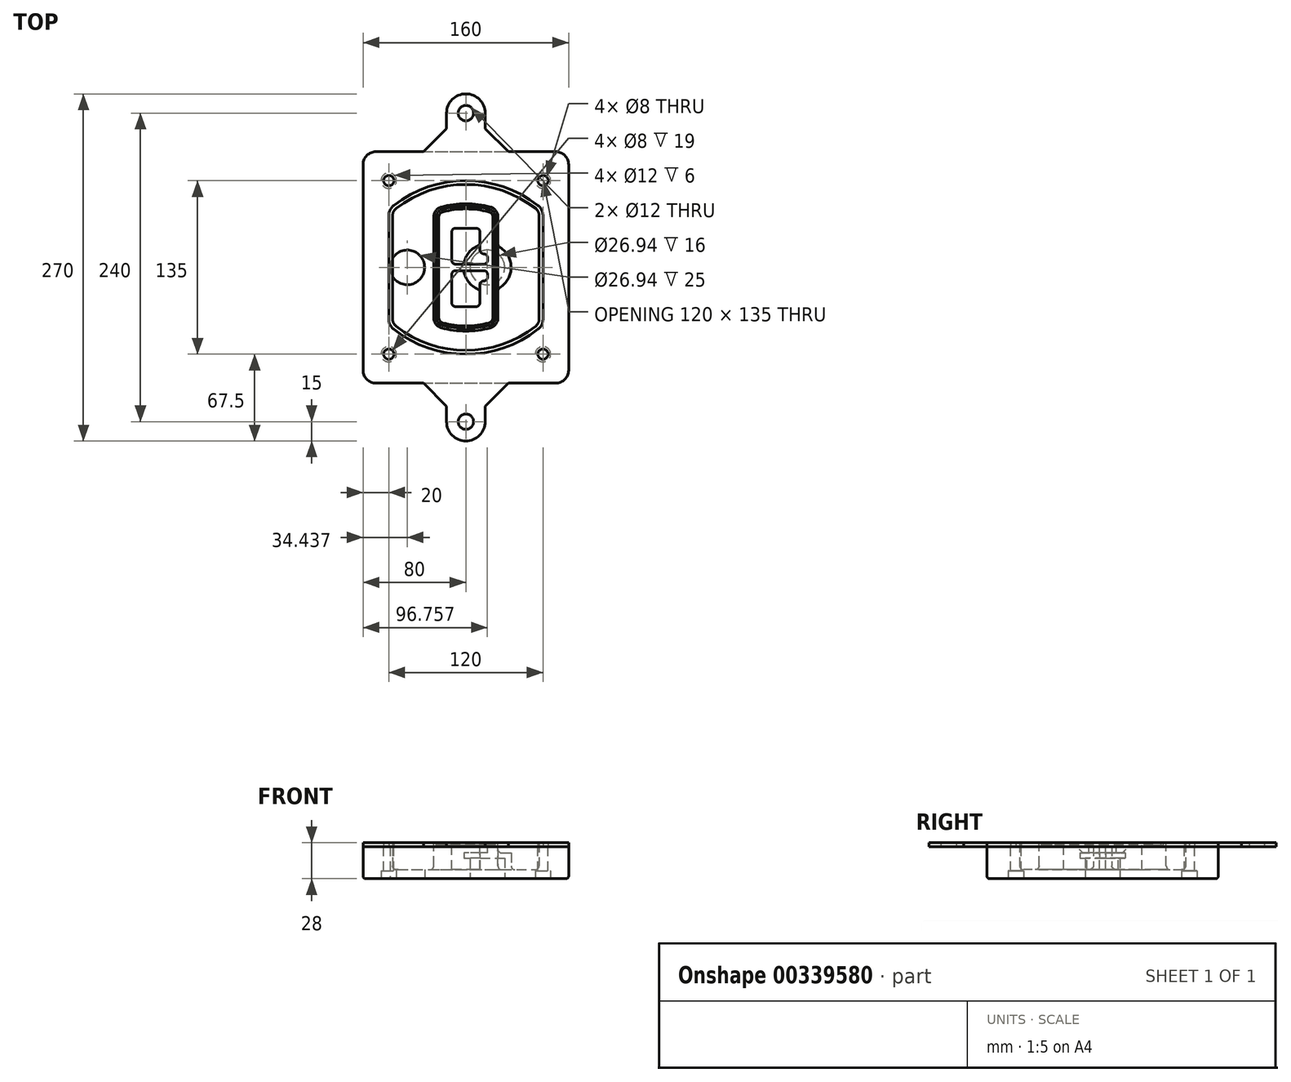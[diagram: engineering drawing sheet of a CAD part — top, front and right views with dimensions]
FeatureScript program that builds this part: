
annotation { "Feature Type Name" : "Feature", "Feature Type Description" : "" }
export const myFeature = defineFeature(function(context is Context, id is Id, definition is map)
    precondition{}
    {
        {
            var Q0;
            Q0=qCreatedBy(makeId("Top.planeOp"),FACE);
            var sketch = newSketch(context, id + "F0", { "sketchPlane" : qUnion([Q0])});
            skPoint(sketch, "E0.rect.middle", {"position": v(0, 0) * mm});
            skLineSegment(sketch, "E1.bottom", {"start": v(-70, -90) * mm, "end": v(70, -90) * mm});
            skLineSegment(sketch, "E1.top", {"start": v(-70, 90) * mm, "end": v(70, 90) * mm});
            skLineSegment(sketch, "E1.left", {"start": v(-80, -80) * mm, "end": v(-80, 80) * mm});
            skLineSegment(sketch, "E1.right", {"start": v(80, -80) * mm, "end": v(80, 80) * mm});
            skLineSegment(sketch, "E2", {"start": v(-80, 90) * mm, "end": v(80, -90) * mm, "construction": true});
            skLineSegment(sketch, "E3", {"start": v(80, 90) * mm, "end": v(-80, -90) * mm, "construction": true});
            skCircle(sketch, "E4", {"center": v(-60, 67.5) * mm, "radius": 4 * mm});
            skCircle(sketch, "E5", {"center": v(60, 67.5) * mm, "radius": 4 * mm});
            skCircle(sketch, "E6", {"center": v(60, -67.5) * mm, "radius": 4 * mm});
            skCircle(sketch, "E7", {"center": v(-60, -67.5) * mm, "radius": 4 * mm});
            skLineSegment(sketch, "E8", {"start": v(-60, 67.5) * mm, "end": v(60, 67.5) * mm, "construction": true});
            skLineSegment(sketch, "E9", {"start": v(60, 67.5) * mm, "end": v(60, -67.5) * mm, "construction": true});
            skLineSegment(sketch, "E10", {"start": v(60, -67.5) * mm, "end": v(-60, -67.5) * mm, "construction": true});
            skLineSegment(sketch, "E11", {"start": v(-60, -67.5) * mm, "end": v(-60, 67.5) * mm, "construction": true});
            skLineSegment(sketch, "E12", {"start": v(-60, 40.3) * mm, "end": v(-60, -40.3) * mm});
            skLineSegment(sketch, "E13", {"start": v(60, 40.3) * mm, "end": v(60, -40.3) * mm});
            skArc(sketch, "E14", {"start": v(56.15, 48.18) * mm, "mid": v(0, 67.5) * mm, "end": v(-56.15, 48.18) * mm});
            skArc(sketch, "E15", {"start": v(-56.15, -48.18) * mm, "mid": v(0, -67.5) * mm, "end": v(56.15, -48.18) * mm});
            skLineSegment(sketch, "E16", {"start": v(-60, 0) * mm, "end": v(60, 0) * mm, "construction": true});
            skPoint(sketch, "E17.visualSharp", {"position": v(-60, -45) * mm});
            skArc(sketch, "E17.filletArc", {"start": v(-60, -40.3) * mm, "mid": v(-58.99, -44.68) * mm, "end": v(-56.15, -48.18) * mm});
            skPoint(sketch, "E18.visualSharp", {"position": v(-60, 45) * mm});
            skArc(sketch, "E18.filletArc", {"start": v(-56.15, 48.18) * mm, "mid": v(-58.99, 44.68) * mm, "end": v(-60, 40.3) * mm});
            skPoint(sketch, "E19.visualSharp", {"position": v(60, 45) * mm});
            skArc(sketch, "E19.filletArc", {"start": v(60, 40.3) * mm, "mid": v(58.99, 44.68) * mm, "end": v(56.15, 48.18) * mm});
            skPoint(sketch, "E20.visualSharp", {"position": v(60, -45) * mm});
            skArc(sketch, "E20.filletArc", {"start": v(56.15, -48.18) * mm, "mid": v(58.99, -44.68) * mm, "end": v(60, -40.3) * mm});
            skPoint(sketch, "E21.visualSharp", {"position": v(-80, 90) * mm});
            skArc(sketch, "E21.filletArc", {"start": v(-70, 90) * mm, "mid": v(-77.07, 87.07) * mm, "end": v(-80, 80) * mm});
            skPoint(sketch, "E22.visualSharp", {"position": v(80, 90) * mm});
            skArc(sketch, "E22.filletArc", {"start": v(80, 80) * mm, "mid": v(77.07, 87.07) * mm, "end": v(70, 90) * mm});
            skPoint(sketch, "E23.visualSharp", {"position": v(80, -90) * mm});
            skArc(sketch, "E23.filletArc", {"start": v(70, -90) * mm, "mid": v(77.07, -87.07) * mm, "end": v(80, -80) * mm});
            skPoint(sketch, "E24.visualSharp", {"position": v(-80, -90) * mm});
            skArc(sketch, "E24.filletArc", {"start": v(-80, -80) * mm, "mid": v(-77.07, -87.07) * mm, "end": v(-70, -90) * mm});
            skArc(sketch, "E25.0", {"start": v(57, 40.3) * mm, "mid": v(56.3, 43.36) * mm, "end": v(54.3, 45.81) * mm});
            skLineSegment(sketch, "E25.1", {"start": v(57, 40.3) * mm, "end": v(57, -40.3) * mm});
            skArc(sketch, "E25.2", {"start": v(54.3, -45.81) * mm, "mid": v(56.3, -43.36) * mm, "end": v(57, -40.3) * mm});
            skArc(sketch, "E25.3", {"start": v(-54.3, -45.81) * mm, "mid": v(0, -64.5) * mm, "end": v(54.3, -45.81) * mm});
            skArc(sketch, "E25.4", {"start": v(-57, -40.3) * mm, "mid": v(-56.3, -43.36) * mm, "end": v(-54.3, -45.81) * mm});
            skArc(sketch, "E25.5", {"start": v(54.3, 45.81) * mm, "mid": v(0, 64.5) * mm, "end": v(-54.3, 45.81) * mm});
            skLineSegment(sketch, "E25.6", {"start": v(-57, 40.3) * mm, "end": v(-57, -40.3) * mm});
            skArc(sketch, "E25.7", {"start": v(-54.3, 45.81) * mm, "mid": v(-56.3, 43.36) * mm, "end": v(-57, 40.3) * mm});
            skArc(sketch, "E26.0", {"start": v(-58.62, 51.33) * mm, "mid": v(-62.58, 46.43) * mm, "end": v(-64, 40.3) * mm});
            skArc(sketch, "E26.1", {"start": v(58.62, 51.33) * mm, "mid": v(0, 71.5) * mm, "end": v(-58.62, 51.33) * mm});
            skArc(sketch, "E26.2", {"start": v(64, 40.3) * mm, "mid": v(62.58, 46.43) * mm, "end": v(58.62, 51.33) * mm});
            skLineSegment(sketch, "E26.3", {"start": v(64, 40.3) * mm, "end": v(64, -40.3) * mm});
            skArc(sketch, "E26.4", {"start": v(58.62, -51.33) * mm, "mid": v(62.58, -46.43) * mm, "end": v(64, -40.3) * mm});
            skLineSegment(sketch, "E26.5", {"start": v(-64, 40.3) * mm, "end": v(-64, -40.3) * mm});
            skArc(sketch, "E26.6", {"start": v(-58.62, -51.33) * mm, "mid": v(0, -71.5) * mm, "end": v(58.62, -51.33) * mm});
            skArc(sketch, "E26.7", {"start": v(-64, -40.3) * mm, "mid": v(-62.58, -46.43) * mm, "end": v(-58.62, -51.33) * mm});
            skSolve(sketch);
        }
        {
            var Q0;
            Q0=makeQuery(id+"F0.imprint","IMPRINT",FACE,{"disambiguationData":[TD([[makeQuery(id+"F0.imprint","IMPRINT",EDGE,{"derivedFrom":sQuery(id+"F0.wireOp",EDGE,"E1.bottom")}),1.0]])]});
            var Q1;
            Q1=makeQuery(id+"F0.imprint","IMPRINT",FACE,{"disambiguationData":[TD([[makeQuery(id+"F0.imprint","IMPRINT",EDGE,{"derivedFrom":sQuery(id+"F0.wireOp",EDGE,"E12")}),1.0]])]});
            var Q2;
            Q2=makeQuery(id+"F0.imprint","IMPRINT",FACE,{"disambiguationData":[TD([[makeQuery(id+"F0.imprint","IMPRINT",EDGE,{"derivedFrom":sQuery(id+"F0.wireOp",EDGE,"E25.0")}),1.0]])]});
            var Q3;
            Q3=makeQuery(id+"F0.imprint","IMPRINT",FACE,{"disambiguationData":[TD([[makeQuery(id+"F0.imprint","IMPRINT",EDGE,{"derivedFrom":sQuery(id+"F0.wireOp",EDGE,"E12")}),-1.0]])]});
            extrude(context, id + "F1", {"entities" : qUnion([Q0, Q1, Q2, Q3]), "oppositeDirection" : true, "depth" : 25 * mm});
        }
        {
            var Q0;
            Q0=makeQuery(id+"F0.imprint","IMPRINT",FACE,{"disambiguationData":[TD([[makeQuery(id+"F0.imprint","IMPRINT",EDGE,{"derivedFrom":sQuery(id+"F0.wireOp",EDGE,"E12")}),1.0]])]});
            extrude(context, id + "F2", {"entities" : qUnion([Q0]), "operationType" : NewBodyOperationType.ADD, "depth" : 3 * mm});
        }
        {
            var Q0;
            Q0=makeQuery(id+"F0.imprint","IMPRINT",FACE,{"disambiguationData":[TD([[makeQuery(id+"F0.imprint","IMPRINT",EDGE,{"derivedFrom":sQuery(id+"F0.wireOp",EDGE,"E25.0")}),1.0]])]});
            extrude(context, id + "F3", {"entities" : qUnion([Q0]), "operationType" : NewBodyOperationType.REMOVE, "oppositeDirection" : true, "depth" : 18 * mm});
        }
        {
            var Q0;
            Q0=makeQuery(id+"F2.opExtrude","CAP_FACE",FACE,{"disambiguationData":[OSD([sQuery(id+"F0.wireOp",EDGE,"E12"),sQuery(id+"F0.wireOp",EDGE,"E13"),sQuery(id+"F0.wireOp",EDGE,"E14"),sQuery(id+"F0.wireOp",EDGE,"E15"),sQuery(id+"F0.wireOp",EDGE,"E17.filletArc"),sQuery(id+"F0.wireOp",EDGE,"E18.filletArc"),sQuery(id+"F0.wireOp",EDGE,"E19.filletArc"),sQuery(id+"F0.wireOp",EDGE,"E20.filletArc"),sQuery(id+"F0.wireOp",EDGE,"E25.0"),sQuery(id+"F0.wireOp",EDGE,"E25.1"),sQuery(id+"F0.wireOp",EDGE,"E25.2"),sQuery(id+"F0.wireOp",EDGE,"E25.3"),sQuery(id+"F0.wireOp",EDGE,"E25.4"),sQuery(id+"F0.wireOp",EDGE,"E25.5"),sQuery(id+"F0.wireOp",EDGE,"E25.6"),sQuery(id+"F0.wireOp",EDGE,"E25.7")])],"isStart":false});
            var sketch = newSketch(context, id + "F4", { "sketchPlane" : qUnion([Q0])});
            skArc(sketch, "E27.0", {"start": v(-19.08, -46.97) * mm, "mid": v(0, -49.5) * mm, "end": v(19.08, -46.97) * mm});
            skArc(sketch, "E28.0", {"start": v(19.08, 46.97) * mm, "mid": v(0, 49.5) * mm, "end": v(-19.08, 46.97) * mm});
            skLineSegment(sketch, "E29", {"start": v(-25, 39.25) * mm, "end": v(-25, -39.25) * mm});
            skLineSegment(sketch, "E30", {"start": v(25, 39.25) * mm, "end": v(25, -39.25) * mm});
            skLineSegment(sketch, "E31", {"start": v(-25, 45.1) * mm, "end": v(25, 45.1) * mm, "construction": true});
            skLineSegment(sketch, "E32", {"start": v(-25, -45.1) * mm, "end": v(25, -45.1) * mm, "construction": true});
            skPoint(sketch, "E33.visualSharp", {"position": v(-25, 45.1) * mm});
            skArc(sketch, "E33.filletArc", {"start": v(-19.08, 46.97) * mm, "mid": v(-23.35, 44.11) * mm, "end": v(-25, 39.25) * mm});
            skPoint(sketch, "E34.visualSharp", {"position": v(25, 45.1) * mm});
            skArc(sketch, "E34.filletArc", {"start": v(25, 39.25) * mm, "mid": v(23.35, 44.11) * mm, "end": v(19.08, 46.97) * mm});
            skPoint(sketch, "E35.visualSharp", {"position": v(25, -45.1) * mm});
            skArc(sketch, "E35.filletArc", {"start": v(19.08, -46.97) * mm, "mid": v(23.35, -44.11) * mm, "end": v(25, -39.25) * mm});
            skPoint(sketch, "E36.visualSharp", {"position": v(-25, -45.1) * mm});
            skArc(sketch, "E36.filletArc", {"start": v(-25, -39.25) * mm, "mid": v(-23.35, -44.11) * mm, "end": v(-19.08, -46.97) * mm});
            skArc(sketch, "E37.0", {"start": v(54.3, 45.81) * mm, "mid": v(0, 64.5) * mm, "end": v(-54.3, 45.81) * mm});
            skArc(sketch, "E37.1", {"start": v(-54.3, 45.81) * mm, "mid": v(-56.3, 43.36) * mm, "end": v(-57, 40.3) * mm});
            skLineSegment(sketch, "E37.2", {"start": v(-57, 40.3) * mm, "end": v(-57, -40.3) * mm});
            skArc(sketch, "E37.3", {"start": v(-57, -40.3) * mm, "mid": v(-56.3, -43.36) * mm, "end": v(-54.3, -45.81) * mm});
            skArc(sketch, "E37.4", {"start": v(-54.3, -45.81) * mm, "mid": v(0, -64.5) * mm, "end": v(54.3, -45.81) * mm});
            skArc(sketch, "E37.5", {"start": v(54.3, -45.81) * mm, "mid": v(56.3, -43.36) * mm, "end": v(57, -40.3) * mm});
            skLineSegment(sketch, "E37.6", {"start": v(57, 40.3) * mm, "end": v(57, -40.3) * mm});
            skArc(sketch, "E37.7", {"start": v(57, 40.3) * mm, "mid": v(56.3, 43.36) * mm, "end": v(54.3, 45.81) * mm});
            skLineSegment(sketch, "E38.0", {"start": v(23, 39.25) * mm, "end": v(23, -39.25) * mm});
            skArc(sketch, "E38.1", {"start": v(18.56, -45.04) * mm, "mid": v(21.76, -42.9) * mm, "end": v(23, -39.25) * mm});
            skArc(sketch, "E38.2", {"start": v(-18.56, -45.04) * mm, "mid": v(0, -47.5) * mm, "end": v(18.56, -45.04) * mm});
            skArc(sketch, "E38.3", {"start": v(-23, -39.25) * mm, "mid": v(-21.76, -42.9) * mm, "end": v(-18.56, -45.04) * mm});
            skLineSegment(sketch, "E38.4", {"start": v(-23, 39.25) * mm, "end": v(-23, -39.25) * mm});
            skArc(sketch, "E38.5", {"start": v(23, 39.25) * mm, "mid": v(21.76, 42.9) * mm, "end": v(18.56, 45.04) * mm});
            skArc(sketch, "E38.6", {"start": v(-18.56, 45.04) * mm, "mid": v(-21.76, 42.9) * mm, "end": v(-23, 39.25) * mm});
            skArc(sketch, "E38.7", {"start": v(18.56, 45.04) * mm, "mid": v(0, 47.5) * mm, "end": v(-18.56, 45.04) * mm});
            skArc(sketch, "E39.0", {"start": v(21, 39.25) * mm, "mid": v(20.18, 41.68) * mm, "end": v(18.04, 43.1) * mm});
            skLineSegment(sketch, "E39.1", {"start": v(21, 39.25) * mm, "end": v(21, -39.25) * mm});
            skArc(sketch, "E39.2", {"start": v(18.04, -43.1) * mm, "mid": v(20.18, -41.68) * mm, "end": v(21, -39.25) * mm});
            skArc(sketch, "E39.3", {"start": v(-18.04, -43.1) * mm, "mid": v(0, -45.5) * mm, "end": v(18.04, -43.1) * mm});
            skArc(sketch, "E39.4", {"start": v(-21, -39.25) * mm, "mid": v(-20.18, -41.68) * mm, "end": v(-18.04, -43.1) * mm});
            skArc(sketch, "E39.5", {"start": v(18.04, 43.1) * mm, "mid": v(0, 45.5) * mm, "end": v(-18.04, 43.1) * mm});
            skLineSegment(sketch, "E39.6", {"start": v(-21, 39.25) * mm, "end": v(-21, -39.25) * mm});
            skArc(sketch, "E39.7", {"start": v(-18.04, 43.1) * mm, "mid": v(-20.18, 41.68) * mm, "end": v(-21, 39.25) * mm});
            skLineSegment(sketch, "E40", {"start": v(-25, 0) * mm, "end": v(25, 0) * mm, "construction": true});
            skLineSegment(sketch, "E41", {"start": v(-11, 5.5) * mm, "end": v(-11, 27.5) * mm});
            skLineSegment(sketch, "E42", {"start": v(-8, 30.5) * mm, "end": v(8, 30.5) * mm});
            skLineSegment(sketch, "E43", {"start": v(11, 27.5) * mm, "end": v(11, 13.5) * mm});
            skLineSegment(sketch, "E44", {"start": v(14, 10.5) * mm, "end": v(14, 10.5) * mm});
            skLineSegment(sketch, "E45", {"start": v(17, 7.5) * mm, "end": v(17, 5.5) * mm});
            skLineSegment(sketch, "E46", {"start": v(14, 2.5) * mm, "end": v(-8, 2.5) * mm});
            skPoint(sketch, "E47.visualSharp", {"position": v(-11, 30.5) * mm});
            skArc(sketch, "E47.filletArc", {"start": v(-8, 30.5) * mm, "mid": v(-10.12, 29.62) * mm, "end": v(-11, 27.5) * mm});
            skPoint(sketch, "E48.visualSharp", {"position": v(11, 30.5) * mm});
            skArc(sketch, "E48.filletArc", {"start": v(11, 27.5) * mm, "mid": v(10.12, 29.62) * mm, "end": v(8, 30.5) * mm});
            skPoint(sketch, "E49.visualSharp", {"position": v(11, 10.5) * mm});
            skArc(sketch, "E49.filletArc", {"start": v(11, 13.5) * mm, "mid": v(11.88, 11.38) * mm, "end": v(14, 10.5) * mm});
            skPoint(sketch, "E50.visualSharp", {"position": v(17, 10.5) * mm});
            skArc(sketch, "E50.filletArc", {"start": v(17, 7.5) * mm, "mid": v(16.12, 9.62) * mm, "end": v(14, 10.5) * mm});
            skPoint(sketch, "E51.visualSharp", {"position": v(17, 2.5) * mm});
            skArc(sketch, "E51.filletArc", {"start": v(14, 2.5) * mm, "mid": v(16.12, 3.38) * mm, "end": v(17, 5.5) * mm});
            skPoint(sketch, "E52.visualSharp", {"position": v(-11, 2.5) * mm});
            skArc(sketch, "E52.filletArc", {"start": v(-11, 5.5) * mm, "mid": v(-10.12, 3.38) * mm, "end": v(-8, 2.5) * mm});
            skLineSegment(sketch, "E53.0.MirrorCS", {"start": v(14, -2.5) * mm, "end": v(-8, -2.5) * mm});
            skArc(sketch, "E54.0.MirrorCS", {"start": v(-11, -5.5) * mm, "mid": v(-10.12, -3.38) * mm, "end": v(-8, -2.5) * mm});
            skLineSegment(sketch, "E55.0.MirrorCS", {"start": v(-11, -5.5) * mm, "end": v(-11, -27.5) * mm});
            skArc(sketch, "E56.0.MirrorCS", {"start": v(-8, -30.5) * mm, "mid": v(-10.12, -29.62) * mm, "end": v(-11, -27.5) * mm});
            skLineSegment(sketch, "E57.0.MirrorCS", {"start": v(-8, -30.5) * mm, "end": v(8, -30.5) * mm});
            skArc(sketch, "E58.0.MirrorCS", {"start": v(11, -27.5) * mm, "mid": v(10.12, -29.62) * mm, "end": v(8, -30.5) * mm});
            skLineSegment(sketch, "E59.0.MirrorCS", {"start": v(11, -27.5) * mm, "end": v(11, -13.5) * mm});
            skArc(sketch, "E60.0.MirrorCS", {"start": v(11, -13.5) * mm, "mid": v(11.88, -11.38) * mm, "end": v(14, -10.5) * mm});
            skArc(sketch, "E61.0.MirrorCS", {"start": v(17, -7.5) * mm, "mid": v(16.12, -9.62) * mm, "end": v(14, -10.5) * mm});
            skLineSegment(sketch, "E62.0.MirrorCS", {"start": v(17, -7.5) * mm, "end": v(17, -5.5) * mm});
            skArc(sketch, "E63.0.MirrorCS", {"start": v(14, -2.5) * mm, "mid": v(16.12, -3.38) * mm, "end": v(17, -5.5) * mm});
            skSolve(sketch);
        }
        {
            var Q0;
            Q0=makeQuery(id+"F4.imprint","IMPRINT",FACE,{"disambiguationData":[TD([[makeQuery(id+"F4.imprint","IMPRINT",EDGE,{"derivedFrom":sQuery(id+"F4.wireOp",EDGE,"E27.0")}),1.0]])]});
            var Q1;
            Q1=makeQuery(id+"F4.imprint","IMPRINT",FACE,{"disambiguationData":[TD([[makeQuery(id+"F4.imprint","IMPRINT",EDGE,{"derivedFrom":sQuery(id+"F4.wireOp",EDGE,"E38.0")}),-1.0]])]});
            var Q2;
            Q2=makeQuery(id+"F4.imprint","IMPRINT",FACE,{"disambiguationData":[TD([[makeQuery(id+"F4.imprint","IMPRINT",EDGE,{"derivedFrom":sQuery(id+"F4.wireOp",EDGE,"E39.0")}),1.0]])]});
            extrude(context, id + "F5", {"entities" : qUnion([Q0, Q1, Q2]), "operationType" : NewBodyOperationType.ADD, "endBound" : BoundingType.UP_TO_NEXT, "oppositeDirection" : true, "depth" : 25 * mm});
        }
        {
            var Q0;
            Q0=makeQuery(id+"F4.imprint","IMPRINT",FACE,{"disambiguationData":[TD([[makeQuery(id+"F4.imprint","IMPRINT",EDGE,{"derivedFrom":sQuery(id+"F4.wireOp",EDGE,"E38.0")}),-1.0]])]});
            extrude(context, id + "F6", {"entities" : qUnion([Q0]), "operationType" : NewBodyOperationType.REMOVE, "oppositeDirection" : true, "depth" : 2 * mm});
        }
        {
            var Q0;
            Q0=makeQuery(id+"F1.opExtrude","CAP_FACE",FACE,{"disambiguationData":[OSD([sQuery(id+"F0.wireOp",EDGE,"E1.bottom"),sQuery(id+"F0.wireOp",EDGE,"E1.top"),sQuery(id+"F0.wireOp",EDGE,"E1.left"),sQuery(id+"F0.wireOp",EDGE,"E1.right"),sQuery(id+"F0.wireOp",EDGE,"E4"),sQuery(id+"F0.wireOp",EDGE,"E5"),sQuery(id+"F0.wireOp",EDGE,"E6"),sQuery(id+"F0.wireOp",EDGE,"E7"),sQuery(id+"F0.wireOp",EDGE,"E21.filletArc"),sQuery(id+"F0.wireOp",EDGE,"E22.filletArc"),sQuery(id+"F0.wireOp",EDGE,"E23.filletArc"),sQuery(id+"F0.wireOp",EDGE,"E24.filletArc")])],"isStart":false});
            var sketch = newSketch(context, id + "F7", { "sketchPlane" : qUnion([Q0])});
            skCircle(sketch, "E64", {"center": v(16.76, 0) * mm, "radius": 13.47 * mm});
            skCircle(sketch, "E65", {"center": v(-45.56, 0) * mm, "radius": 13.47 * mm});
            skLineSegment(sketch, "E66", {"start": v(80, 0) * mm, "end": v(-80, 0) * mm});
            skCircle(sketch, "E67", {"center": v(16.76, 0) * mm, "radius": 18.47 * mm});
            skCircle(sketch, "E68", {"center": v(60, -67.5) * mm, "radius": 6 * mm});
            skCircle(sketch, "E69", {"center": v(-60, -67.5) * mm, "radius": 6 * mm});
            skCircle(sketch, "E70", {"center": v(-60, 67.5) * mm, "radius": 6 * mm});
            skCircle(sketch, "E71", {"center": v(60, 67.5) * mm, "radius": 6 * mm});
            skSolve(sketch);
        }
        {
            var Q0;
            {var subQ1=sQuery(id+"F7.wireOp",EDGE,"E66");var subQ4=sQuery(id+"F7.wireOp",EDGE,"E64");var subQ6=makeQuery(id+"F7.imprint","INTERSECT",VERTEX,{"disambiguationData":[OD(0.0)],"derivedFrom":[subQ4,subQ1]});Q0=makeQuery(id+"F7.imprint","IMPRINT",FACE,{"disambiguationData":[TD([[makeQuery(id+"F7.imprint","IMPRINT",EDGE,{"disambiguationData":[TD([[subQ6,-1.0]])],"derivedFrom":subQ4}),-1.0]])]});}
            var Q1;
            {var subQ0=sQuery(id+"F7.wireOp",EDGE,"E66");var subQ1=sQuery(id+"F7.wireOp",EDGE,"E64");var subQ3=makeQuery(id+"F7.imprint","INTERSECT",VERTEX,{"disambiguationData":[OD(0.0)],"derivedFrom":[subQ1,subQ0]});Q1=makeQuery(id+"F7.imprint","IMPRINT",FACE,{"disambiguationData":[TD([[makeQuery(id+"F7.imprint","IMPRINT",EDGE,{"disambiguationData":[TD([[subQ3,-1.0]])],"derivedFrom":subQ1}),1.0]])]});}
            var Q2;
            {var subQ0=sQuery(id+"F7.wireOp",EDGE,"E66");var subQ1=sQuery(id+"F7.wireOp",EDGE,"E64");var subQ3=makeQuery(id+"F7.imprint","INTERSECT",VERTEX,{"disambiguationData":[OD(0.0)],"derivedFrom":[subQ1,subQ0]});Q2=makeQuery(id+"F7.imprint","IMPRINT",FACE,{"disambiguationData":[TD([[makeQuery(id+"F7.imprint","IMPRINT",EDGE,{"disambiguationData":[TD([[subQ3,1.0]])],"derivedFrom":subQ1}),1.0]])]});}
            var Q3;
            {var subQ1=sQuery(id+"F7.wireOp",EDGE,"E66");var subQ4=sQuery(id+"F7.wireOp",EDGE,"E64");var subQ6=makeQuery(id+"F7.imprint","INTERSECT",VERTEX,{"disambiguationData":[OD(0.0)],"derivedFrom":[subQ4,subQ1]});Q3=makeQuery(id+"F7.imprint","IMPRINT",FACE,{"disambiguationData":[TD([[makeQuery(id+"F7.imprint","IMPRINT",EDGE,{"disambiguationData":[TD([[subQ6,1.0]])],"derivedFrom":subQ4}),-1.0]])]});}
            extrude(context, id + "F8", {"entities" : qUnion([Q0, Q1, Q2, Q3]), "operationType" : NewBodyOperationType.ADD, "oppositeDirection" : true, "depth" : 20 * mm});
        }
        {
            var Q0;
            {var subQ0=sQuery(id+"F7.wireOp",EDGE,"E66");var subQ1=sQuery(id+"F7.wireOp",EDGE,"E64");var subQ3=makeQuery(id+"F7.imprint","INTERSECT",VERTEX,{"disambiguationData":[OD(0.0)],"derivedFrom":[subQ1,subQ0]});Q0=makeQuery(id+"F7.imprint","IMPRINT",FACE,{"disambiguationData":[TD([[makeQuery(id+"F7.imprint","IMPRINT",EDGE,{"disambiguationData":[TD([[subQ3,-1.0]])],"derivedFrom":subQ1}),1.0]])]});}
            var Q1;
            {var subQ0=sQuery(id+"F7.wireOp",EDGE,"E66");var subQ1=sQuery(id+"F7.wireOp",EDGE,"E64");var subQ3=makeQuery(id+"F7.imprint","INTERSECT",VERTEX,{"disambiguationData":[OD(0.0)],"derivedFrom":[subQ1,subQ0]});Q1=makeQuery(id+"F7.imprint","IMPRINT",FACE,{"disambiguationData":[TD([[makeQuery(id+"F7.imprint","IMPRINT",EDGE,{"disambiguationData":[TD([[subQ3,1.0]])],"derivedFrom":subQ1}),1.0]])]});}
            extrude(context, id + "F9", {"entities" : qUnion([Q0, Q1]), "operationType" : NewBodyOperationType.REMOVE, "oppositeDirection" : true, "depth" : 16 * mm});
        }
        {
            var Q0;
            {var subQ0=sQuery(id+"F7.wireOp",EDGE,"E66");var subQ1=sQuery(id+"F7.wireOp",EDGE,"E65");var subQ3=makeQuery(id+"F7.imprint","INTERSECT",VERTEX,{"disambiguationData":[OD(0.0)],"derivedFrom":[subQ1,subQ0]});Q0=makeQuery(id+"F7.imprint","IMPRINT",FACE,{"disambiguationData":[TD([[makeQuery(id+"F7.imprint","IMPRINT",EDGE,{"disambiguationData":[TD([[subQ3,-1.0]])],"derivedFrom":subQ1}),1.0]])]});}
            var Q1;
            {var subQ0=sQuery(id+"F7.wireOp",EDGE,"E66");var subQ1=sQuery(id+"F7.wireOp",EDGE,"E65");var subQ3=makeQuery(id+"F7.imprint","INTERSECT",VERTEX,{"disambiguationData":[OD(0.0)],"derivedFrom":[subQ1,subQ0]});Q1=makeQuery(id+"F7.imprint","IMPRINT",FACE,{"disambiguationData":[TD([[makeQuery(id+"F7.imprint","IMPRINT",EDGE,{"disambiguationData":[TD([[subQ3,1.0]])],"derivedFrom":subQ1}),1.0]])]});}
            extrude(context, id + "F10", {"entities" : qUnion([Q0, Q1]), "operationType" : NewBodyOperationType.REMOVE, "oppositeDirection" : true, "depth" : 25 * mm});
        }
        {
            var Q0;
            Q0=makeQuery(id+"F7.imprint","IMPRINT",FACE,{"disambiguationData":[TD([[makeQuery(id+"F7.imprint","IMPRINT",EDGE,{"derivedFrom":sQuery(id+"F7.wireOp",EDGE,"E68")}),1.0]])]});
            var Q1;
            Q1=makeQuery(id+"F7.imprint","IMPRINT",FACE,{"disambiguationData":[TD([[makeQuery(id+"F7.imprint","IMPRINT",EDGE,{"derivedFrom":makeQuery(id+"F1.opExtrude","CAP_EDGE",EDGE,{"disambiguationData":[OSD([sQuery(id+"F0.wireOp",EDGE,"E5")])],"isStart":false})}),-1.0]])]});
            var Q2;
            Q2=makeQuery(id+"F7.imprint","IMPRINT",FACE,{"disambiguationData":[TD([[makeQuery(id+"F7.imprint","IMPRINT",EDGE,{"derivedFrom":sQuery(id+"F7.wireOp",EDGE,"E69")}),1.0]])]});
            var Q3;
            Q3=makeQuery(id+"F7.imprint","IMPRINT",FACE,{"disambiguationData":[TD([[makeQuery(id+"F7.imprint","IMPRINT",EDGE,{"derivedFrom":makeQuery(id+"F1.opExtrude","CAP_EDGE",EDGE,{"disambiguationData":[OSD([sQuery(id+"F0.wireOp",EDGE,"E4")])],"isStart":false})}),-1.0]])]});
            var Q4;
            Q4=makeQuery(id+"F7.imprint","IMPRINT",FACE,{"disambiguationData":[TD([[makeQuery(id+"F7.imprint","IMPRINT",EDGE,{"derivedFrom":sQuery(id+"F7.wireOp",EDGE,"E70")}),1.0]])]});
            var Q5;
            Q5=makeQuery(id+"F7.imprint","IMPRINT",FACE,{"disambiguationData":[TD([[makeQuery(id+"F7.imprint","IMPRINT",EDGE,{"derivedFrom":makeQuery(id+"F1.opExtrude","CAP_EDGE",EDGE,{"disambiguationData":[OSD([sQuery(id+"F0.wireOp",EDGE,"E7")])],"isStart":false})}),-1.0]])]});
            var Q6;
            Q6=makeQuery(id+"F7.imprint","IMPRINT",FACE,{"disambiguationData":[TD([[makeQuery(id+"F7.imprint","IMPRINT",EDGE,{"derivedFrom":sQuery(id+"F7.wireOp",EDGE,"E71")}),1.0]])]});
            var Q7;
            Q7=makeQuery(id+"F7.imprint","IMPRINT",FACE,{"disambiguationData":[TD([[makeQuery(id+"F7.imprint","IMPRINT",EDGE,{"derivedFrom":makeQuery(id+"F1.opExtrude","CAP_EDGE",EDGE,{"disambiguationData":[OSD([sQuery(id+"F0.wireOp",EDGE,"E6")])],"isStart":false})}),-1.0]])]});
            extrude(context, id + "F11", {"entities" : qUnion([Q0, Q1, Q2, Q3, Q4, Q5, Q6, Q7]), "operationType" : NewBodyOperationType.REMOVE, "oppositeDirection" : true, "depth" : 6 * mm});
        }
        {
            var Q0;
            Q0=makeQuery(id+"F9.boolean.opBoolean","COPY",FACE,{"derivedFrom":makeQuery(id+"F9.opExtrude","CAP_FACE",FACE,{"disambiguationData":[OSD([sQuery(id+"F7.wireOp",EDGE,"E64")])],"isStart":false})});
            var sketch = newSketch(context, id + "F12", { "sketchPlane" : qUnion([Q0])});
            skArc(sketch, "E72.0", {"start": v(11, 17.55) * mm, "mid": v(2.57, 11.82) * mm, "end": v(-1.54, 2.5) * mm});
            skArc(sketch, "E72.1", {"start": v(-1.54, -2.5) * mm, "mid": v(2.57, -11.82) * mm, "end": v(11, -17.55) * mm});
            skLineSegment(sketch, "E73", {"start": v(-1.54, -2.5) * mm, "end": v(14, -2.5) * mm});
            skLineSegment(sketch, "E74.0", {"start": v(14, 2.5) * mm, "end": v(-1.54, 2.5) * mm});
            skArc(sketch, "E74.1", {"start": v(14, 2.5) * mm, "mid": v(16.12, 3.38) * mm, "end": v(17, 5.5) * mm});
            skLineSegment(sketch, "E74.2", {"start": v(17, 7.5) * mm, "end": v(17, 5.5) * mm});
            skArc(sketch, "E74.3", {"start": v(17, 7.5) * mm, "mid": v(16.12, 9.62) * mm, "end": v(14, 10.5) * mm});
            skArc(sketch, "E74.4", {"start": v(11, 13.5) * mm, "mid": v(11.88, 11.38) * mm, "end": v(14, 10.5) * mm});
            skLineSegment(sketch, "E74.5", {"start": v(11, 17.55) * mm, "end": v(11, 13.5) * mm});
            skLineSegment(sketch, "E74.7", {"start": v(14, -2.5) * mm, "end": v(-1.54, -2.5) * mm});
            skArc(sketch, "E74.8", {"start": v(14, -2.5) * mm, "mid": v(16.12, -3.38) * mm, "end": v(17, -5.5) * mm});
            skLineSegment(sketch, "E74.9", {"start": v(17, -7.5) * mm, "end": v(17, -5.5) * mm});
            skArc(sketch, "E74.10", {"start": v(17, -7.5) * mm, "mid": v(16.12, -9.62) * mm, "end": v(14, -10.5) * mm});
            skArc(sketch, "E74.11", {"start": v(11, -13.5) * mm, "mid": v(11.88, -11.38) * mm, "end": v(14, -10.5) * mm});
            skLineSegment(sketch, "E74.12", {"start": v(11, -17.55) * mm, "end": v(11, -13.5) * mm});
            skPoint(sketch, "E75.orphan", {"position": v(11, -27.5) * mm});
            skPoint(sketch, "E76.orphan", {"position": v(-8, -2.5) * mm});
            skPoint(sketch, "E77.orphan", {"position": v(-8, 2.5) * mm});
            skPoint(sketch, "E78.orphan", {"position": v(11, 27.5) * mm});
            skSolve(sketch);
        }
        {
            var Q0;
            {var subQ7=sQuery(id+"F12.wireOp",EDGE,"E72.0");var subQ14=sQuery(id+"F12.wireOp",EDGE,"E72.1");var subQ16=sQuery(id+"F12.wireOp",EDGE,"E74.1");var subQ18=sQuery(id+"F12.wireOp",EDGE,"E74.8");Q0=qUnion([makeQuery(id+"F12.imprint","IMPRINT",FACE,{"disambiguationData":[TD([[makeQuery(id+"F12.imprint","IMPRINT",EDGE,{"derivedFrom":subQ7}),1.0]])]}),makeQuery(id+"F12.imprint","IMPRINT",FACE,{"disambiguationData":[TD([[makeQuery(id+"F12.imprint","IMPRINT",EDGE,{"derivedFrom":subQ14}),1.0]])]}),makeQuery(id+"F12.imprint","IMPRINT",FACE,{"disambiguationData":[TD([[makeQuery(id+"F12.imprint","IMPRINT",EDGE,{"derivedFrom":subQ16}),1.0]])]}),makeQuery(id+"F12.imprint","IMPRINT",FACE,{"disambiguationData":[TD([[makeQuery(id+"F12.imprint","IMPRINT",EDGE,{"derivedFrom":subQ18}),-1.0]])]})]);}
            var Q1;
            Q1=makeQuery(id+"F5.boolean.opBoolean","SPLIT",FACE,{"disambiguationData":[TD([makeQuery(id+"F5.opExtrude","SWEPT_FACE",FACE,{"disambiguationData":[OSD([sQuery(id+"F4.wireOp",EDGE,"E41")])]})])],"derivedFrom":makeQuery(id+"F3.boolean.opBoolean","COPY",FACE,{"derivedFrom":makeQuery(id+"F3.opExtrude","CAP_FACE",FACE,{"disambiguationData":[OSD([sQuery(id+"F0.wireOp",EDGE,"E25.0"),sQuery(id+"F0.wireOp",EDGE,"E25.1"),sQuery(id+"F0.wireOp",EDGE,"E25.2"),sQuery(id+"F0.wireOp",EDGE,"E25.3"),sQuery(id+"F0.wireOp",EDGE,"E25.4"),sQuery(id+"F0.wireOp",EDGE,"E25.5"),sQuery(id+"F0.wireOp",EDGE,"E25.6"),sQuery(id+"F0.wireOp",EDGE,"E25.7")])],"isStart":false})})});
            extrude(context, id + "F13", {"entities" : qUnion([Q0]), "operationType" : NewBodyOperationType.REMOVE, "endBound" : BoundingType.UP_TO_SURFACE, "endBoundEntityFace" : qUnion([Q1]), "depth" : 25 * mm});
        }
        {
            var Q0;
            Q0=makeQuery(id+"F3.boolean.opBoolean","COPY",EDGE,{"derivedFrom":makeQuery(id+"F3.opExtrude","CAP_EDGE",EDGE,{"disambiguationData":[OSD([sQuery(id+"F0.wireOp",EDGE,"E25.6")])],"isStart":false})});
            var Q1;
            Q1=makeQuery(id+"F8.boolean.opBoolean","INTERSECT",EDGE,{"derivedFrom":[makeQuery(id+"F5.opExtrude","SWEPT_FACE",FACE,{"disambiguationData":[OSD([sQuery(id+"F4.wireOp",EDGE,"E30")])]}),makeQuery(id+"F8.opExtrude","CAP_FACE",FACE,{"disambiguationData":[OSD([sQuery(id+"F7.wireOp",EDGE,"E67")])],"isStart":false})]});
            var Q2;
            Q2=makeQuery(id+"F8.boolean.opBoolean","INTERSECT",EDGE,{"disambiguationData":[OD(1.0)],"derivedFrom":[makeQuery(id+"F5.opExtrude","SWEPT_FACE",FACE,{"disambiguationData":[OSD([sQuery(id+"F4.wireOp",EDGE,"E30")])]}),makeQuery(id+"F8.opExtrude","SWEPT_FACE",FACE,{"disambiguationData":[OSD([sQuery(id+"F7.wireOp",EDGE,"E67")])]})]});
            var Q3;
            {var subQ0=sQuery(id+"F4.wireOp",EDGE,"E30");Q3=makeQuery(id+"F8.boolean.opBoolean","SPLIT",EDGE,{"disambiguationData":[TD([makeQuery(id+"F5.opExtrude","SWEPT_FACE",FACE,{"disambiguationData":[OSD([sQuery(id+"F4.wireOp",EDGE,"E35.filletArc")])]})])],"derivedFrom":makeQuery(id+"F5.opExtrude","CAP_EDGE",EDGE,{"disambiguationData":[OSD([subQ0])],"isStart":false})});}
            var Q4;
            {var subQ0=sQuery(id+"F0.wireOp",EDGE,"E25.7");var subQ1=sQuery(id+"F0.wireOp",EDGE,"E25.1");var subQ2=sQuery(id+"F0.wireOp",EDGE,"E25.6");var subQ3=sQuery(id+"F0.wireOp",EDGE,"E25.5");var subQ4=sQuery(id+"F0.wireOp",EDGE,"E25.4");var subQ5=sQuery(id+"F0.wireOp",EDGE,"E25.0");var subQ6=sQuery(id+"F0.wireOp",EDGE,"E25.2");var subQ7=sQuery(id+"F0.wireOp",EDGE,"E25.3");Q4=makeQuery(id+"F8.boolean.opBoolean","INTERSECT",EDGE,{"derivedFrom":[makeQuery(id+"F5.boolean.opBoolean","SPLIT",FACE,{"disambiguationData":[TD([makeQuery(id+"F2.opExtrude","SWEPT_FACE",FACE,{"disambiguationData":[OSD([subQ5])]})])],"derivedFrom":makeQuery(id+"F3.boolean.opBoolean","COPY",FACE,{"derivedFrom":makeQuery(id+"F3.opExtrude","CAP_FACE",FACE,{"disambiguationData":[OSD([subQ5,subQ1,subQ6,subQ7,subQ4,subQ3,subQ2,subQ0])],"isStart":false})})}),makeQuery(id+"F8.opExtrude","SWEPT_FACE",FACE,{"disambiguationData":[OSD([sQuery(id+"F7.wireOp",EDGE,"E67")])]})]});}
            var Q5;
            Q5=makeQuery(id+"F8.boolean.opBoolean","INTERSECT",EDGE,{"disambiguationData":[OD(0.0)],"derivedFrom":[makeQuery(id+"F5.opExtrude","SWEPT_FACE",FACE,{"disambiguationData":[OSD([sQuery(id+"F4.wireOp",EDGE,"E30")])]}),makeQuery(id+"F8.opExtrude","SWEPT_FACE",FACE,{"disambiguationData":[OSD([sQuery(id+"F7.wireOp",EDGE,"E67")])]})]});
            fillet(context, id + "F14", {"entities" : qUnion([Q0, Q1, Q2, Q3, Q4, Q5]), "radius" : 3 * mm, "tangentPropagation" : true, "allowEdgeOverflow" : false});
        }
        {
            var Q0;
            Q0=makeQuery(id+"F1.opExtrude","CAP_EDGE",EDGE,{"disambiguationData":[OSD([sQuery(id+"F0.wireOp",EDGE,"E1.bottom")])],"isStart":false});
            fillet(context, id + "F15", {"entities" : qUnion([Q0]), "radius" : 2 * mm, "tangentPropagation" : true, "allowEdgeOverflow" : false});
        }
        {
            var Q0;
            {var subQ0=sQuery(id+"F0.wireOp",EDGE,"E21.filletArc");var subQ1=sQuery(id+"F0.wireOp",EDGE,"E7");var subQ2=sQuery(id+"F0.wireOp",EDGE,"E6");var subQ3=sQuery(id+"F0.wireOp",EDGE,"E5");var subQ4=sQuery(id+"F0.wireOp",EDGE,"E4");var subQ5=sQuery(id+"F0.wireOp",EDGE,"E22.filletArc");var subQ6=sQuery(id+"F0.wireOp",EDGE,"E1.bottom");var subQ7=sQuery(id+"F0.wireOp",EDGE,"E1.right");var subQ8=sQuery(id+"F0.wireOp",EDGE,"E1.top");var subQ9=sQuery(id+"F0.wireOp",EDGE,"E1.left");var subQ10=sQuery(id+"F0.wireOp",EDGE,"E23.filletArc");var subQ11=sQuery(id+"F0.wireOp",EDGE,"E24.filletArc");Q0=makeQuery(id+"F2.boolean.opBoolean","SPLIT",FACE,{"disambiguationData":[TD([makeQuery(id+"F1.opExtrude","SWEPT_FACE",FACE,{"disambiguationData":[OSD([subQ6])]})])],"derivedFrom":makeQuery(id+"F1.opExtrude","CAP_FACE",FACE,{"disambiguationData":[OSD([subQ6,subQ8,subQ9,subQ7,subQ4,subQ3,subQ2,subQ1,subQ0,subQ5,subQ10,subQ11])],"isStart":true})});}
            var sketch = newSketch(context, id + "F16", { "sketchPlane" : qUnion([Q0])});
            skLineSegment(sketch, "E79.0", {"start": v(-70, 90) * mm, "end": v(70, 90) * mm});
            skArc(sketch, "E79.1", {"start": v(-70, 90) * mm, "mid": v(-77.07, 87.07) * mm, "end": v(-80, 80) * mm});
            skLineSegment(sketch, "E79.2", {"start": v(-80, -80) * mm, "end": v(-80, 80) * mm});
            skArc(sketch, "E79.3", {"start": v(-80, -80) * mm, "mid": v(-77.07, -87.07) * mm, "end": v(-70, -90) * mm});
            skLineSegment(sketch, "E79.4", {"start": v(-70, -90) * mm, "end": v(70, -90) * mm});
            skArc(sketch, "E79.5", {"start": v(70, -90) * mm, "mid": v(77.07, -87.07) * mm, "end": v(80, -80) * mm});
            skLineSegment(sketch, "E79.6", {"start": v(80, -80) * mm, "end": v(80, 80) * mm});
            skArc(sketch, "E79.7", {"start": v(80, 80) * mm, "mid": v(77.07, 87.07) * mm, "end": v(70, 90) * mm});
            skCircle(sketch, "E79.8", {"center": v(60, 67.5) * mm, "radius": 4 * mm});
            skCircle(sketch, "E79.9", {"center": v(-60, 67.5) * mm, "radius": 4 * mm});
            skCircle(sketch, "E79.10", {"center": v(-60, -67.5) * mm, "radius": 4 * mm});
            skCircle(sketch, "E79.11", {"center": v(60, -67.5) * mm, "radius": 4 * mm});
            skArc(sketch, "E79.12", {"start": v(-56.15, -48.18) * mm, "mid": v(0, -67.5) * mm, "end": v(56.15, -48.18) * mm});
            skArc(sketch, "E79.13", {"start": v(56.15, -48.18) * mm, "mid": v(58.99, -44.68) * mm, "end": v(60, -40.3) * mm});
            skLineSegment(sketch, "E79.14", {"start": v(60, 40.3) * mm, "end": v(60, -40.3) * mm});
            skArc(sketch, "E79.15", {"start": v(-60, -40.3) * mm, "mid": v(-58.99, -44.68) * mm, "end": v(-56.15, -48.18) * mm});
            skLineSegment(sketch, "E79.16", {"start": v(-60, 40.3) * mm, "end": v(-60, -40.3) * mm});
            skArc(sketch, "E79.17", {"start": v(-56.15, 48.18) * mm, "mid": v(-58.99, 44.68) * mm, "end": v(-60, 40.3) * mm});
            skArc(sketch, "E79.18", {"start": v(56.15, 48.18) * mm, "mid": v(0, 67.5) * mm, "end": v(-56.15, 48.18) * mm});
            skArc(sketch, "E79.19", {"start": v(60, 40.3) * mm, "mid": v(58.99, 44.68) * mm, "end": v(56.15, 48.18) * mm});
            skLineSegment(sketch, "E80", {"start": v(0, 120) * mm, "end": v(0, 90) * mm, "construction": true});
            skPoint(sketch, "E80.startSnap0", {"position": v(0, 90) * mm});
            skLineSegment(sketch, "E81", {"start": v(-33, 90) * mm, "end": v(-15, 108) * mm});
            skLineSegment(sketch, "E82", {"start": v(-15, 108) * mm, "end": v(-15, 120) * mm});
            skCircle(sketch, "E83", {"center": v(0, 120) * mm, "radius": 6 * mm});
            skLineSegment(sketch, "E84.MirrorCS", {"start": v(15, 108) * mm, "end": v(15, 120) * mm});
            skLineSegment(sketch, "E85.MirrorCS", {"start": v(33, 90) * mm, "end": v(15, 108) * mm});
            skArc(sketch, "E86", {"start": v(15, 120) * mm, "mid": v(0, 135) * mm, "end": v(-15, 120) * mm});
            skLineSegment(sketch, "E87", {"start": v(-80, 0) * mm, "end": v(80, 0) * mm, "construction": true});
            skLineSegment(sketch, "E88.MirrorCS", {"start": v(-33, -90) * mm, "end": v(-15, -108) * mm});
            skLineSegment(sketch, "E89.MirrorCS", {"start": v(0, -120) * mm, "end": v(0, -90) * mm, "construction": true});
            skLineSegment(sketch, "E90.MirrorCS", {"start": v(-15, -108) * mm, "end": v(-15, -120) * mm});
            skArc(sketch, "E91.MirrorCS", {"start": v(15, -120) * mm, "mid": v(0, -135) * mm, "end": v(-15, -120) * mm});
            skCircle(sketch, "E92.MirrorC", {"center": v(0, -120) * mm, "radius": 6 * mm});
            skLineSegment(sketch, "E93.MirrorCS", {"start": v(15, -108) * mm, "end": v(15, -120) * mm});
            skLineSegment(sketch, "E94.MirrorCS", {"start": v(33, -90) * mm, "end": v(15, -108) * mm});
            skSolve(sketch);
        }
        {
            var Q0;
            Q0 = qSketchRegion(id + "F16", true);
            var Q1;
            Q1=makeQuery(id+"F2.opExtrude","CAP_FACE",FACE,{"disambiguationData":[OSD([sQuery(id+"F0.wireOp",EDGE,"E12"),sQuery(id+"F0.wireOp",EDGE,"E13"),sQuery(id+"F0.wireOp",EDGE,"E14"),sQuery(id+"F0.wireOp",EDGE,"E15"),sQuery(id+"F0.wireOp",EDGE,"E17.filletArc"),sQuery(id+"F0.wireOp",EDGE,"E18.filletArc"),sQuery(id+"F0.wireOp",EDGE,"E19.filletArc"),sQuery(id+"F0.wireOp",EDGE,"E20.filletArc"),sQuery(id+"F0.wireOp",EDGE,"E25.0"),sQuery(id+"F0.wireOp",EDGE,"E25.1"),sQuery(id+"F0.wireOp",EDGE,"E25.2"),sQuery(id+"F0.wireOp",EDGE,"E25.3"),sQuery(id+"F0.wireOp",EDGE,"E25.4"),sQuery(id+"F0.wireOp",EDGE,"E25.5"),sQuery(id+"F0.wireOp",EDGE,"E25.6"),sQuery(id+"F0.wireOp",EDGE,"E25.7")])],"isStart":false});
            extrude(context, id + "F17", {"entities" : qUnion([Q0]), "endBound" : BoundingType.UP_TO_SURFACE, "endBoundEntityFace" : qUnion([Q1]), "depth" : 25 * mm});
        }
    });
